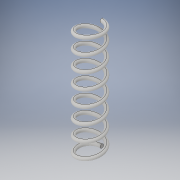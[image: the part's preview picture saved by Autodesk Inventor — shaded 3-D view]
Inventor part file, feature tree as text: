
AUTODESK INVENTOR PART (.ipt)
format: ipt  version: 2019 (Build 230136000, 136)  size: 445,440 bytes
history: native  units: in
note: dims shown in document units (in); Inventor stores cm internally (conversion verified against a paired STEP export)
features: helix x1, sketch x1
ambient origin geometry x8: Origin, YZ Plane, XZ Plane, XY Plane, X Axis, Y Axis, Z Axis, Center Point
bodies: Solid1 (feature_tree)
feature tree (2):
  helix  "Coil1"  [1 undecoded]
  sketch  "Sketch1"  dims[d1=0.0787in d2=1.7717in d3=0.3937in d4=2.3622in d5=2.7559in d6=0.0in d7=90.0deg d8=90.0deg d9=90.0deg d10=90.0deg]
note: 1 required parameter value undecoded (feature->parameter linkage not recoverable at this tier; creation-order binding heuristic only, values carry confidence <= 0.55)
